# Revit family: HL_RU_Basement drain_HL71.1_50-A-171212
name_source: partatom
category: Instalační zařizovací předměty
units: mm (PartAtom-declared; Revit-internal decimal feet)

## family parameters
Bod výpočtu místnosti = Ano
Kóta kulaté spojky = Použít průměr
Nadpis OmniClass = Deck Waste Water Drains
Ořezat dutým tvarem při načtení = Ne
Sdílené = Ano
Typ dílu = Normální
Vždy vertikální = Ano
Založené na pracovní rovině = Ne
Číslo OmniClass = 23.70.50.21.24.14

## types (1)
- HL-Трап для подвалов-HL71.1-50
    EAN = 9003076711505
    Indexovaná poznámka = HL71.1_50
    Komentáře k typům = Трап для подвалов DN110 горизонтальный с входным отверстием DN50, 170х240мм/155х225мм синтетический материал
    Model = HL71.1_50
    Popis = Трап для подвалов
    Přípoj CW = Ne
    Přípoj HW = Ne
    Přípoj odpadních dílů = Ano
    Přípoj ventilace = Ne
    URL = http://www.hutterer-lechner.com
    Výchozí výška = 0 mm  [stored 0 ft]
    Výrobce = HL Hutterer & Lechner GmbH
    ВЕС = 1,43 kg
    ВЫСОТА МОНТАЖА = 220 mm
    МАКСИМАЛЬНАЯ НАГРУЗКА КЛАССА = K3 - 300 kg
    МАТЕРИАЛ = ABS
    НАСАДКА = 170x240 mm
    НОМИНАЛЬНЫЙ ДИАМЕТР = 110 mm
    ПРИЁМНОЕ ОТВЕРСТИЕ = DN50
    ПРОИЗВОДИТЕЛЬНОСТЬ = 2,3 l/s
    РАЗМЕР = DN110
    РЕШЁТКА = 155x225 mm/ ABS

note: [stored X ft] marks values corroborated as IEEE doubles in the binary element streams (Revit-internal decimal feet)

## geometry (parser evidence)
native form markers: Sweep x2
no freeform markers — native parametric forms only
